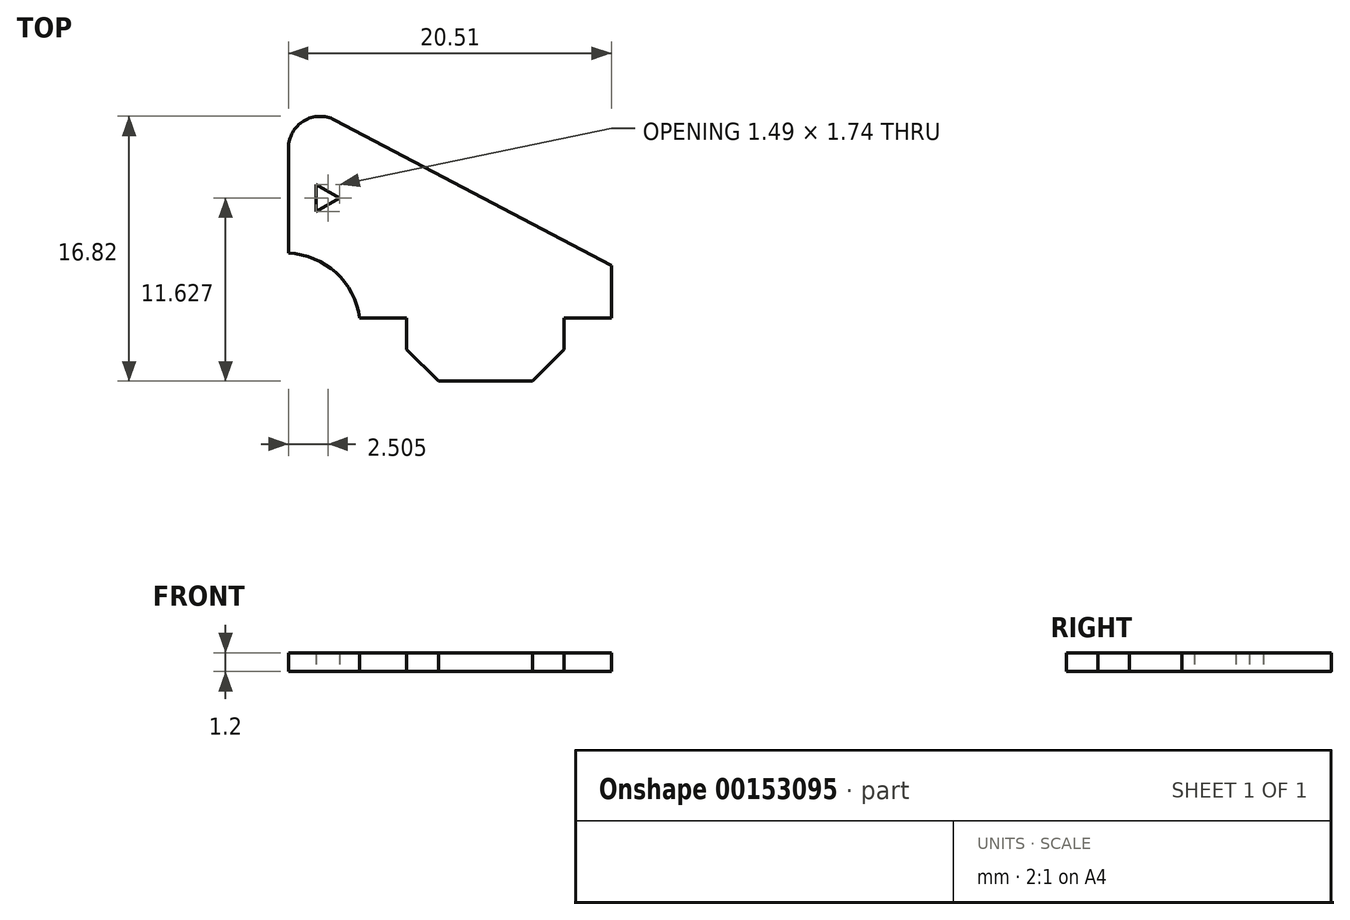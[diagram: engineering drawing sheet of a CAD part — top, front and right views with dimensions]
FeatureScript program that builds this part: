
annotation { "Feature Type Name" : "Feature", "Feature Type Description" : "" }
export const myFeature = defineFeature(function(context is Context, id is Id, definition is map)
    precondition{}
    {
        {
            var Q0;
            Q0=qCreatedBy(makeId("Top.planeOp"),FACE);
            var sketch = newSketch(context, id + "F0", { "sketchPlane" : qUnion([Q0])});
            skLineSegment(sketch, "E0", {"start": v(-14.2, 8.73) * mm, "end": v(-11.2, 8.73) * mm});
            skLineSegment(sketch, "E1", {"start": v(-11.2, 8.73) * mm, "end": v(-11.2, 6.73) * mm});
            skLineSegment(sketch, "E2", {"start": v(-11.2, 6.73) * mm, "end": v(-11.2, 4.73) * mm, "construction": true});
            skLineSegment(sketch, "E3", {"start": v(-11.2, 4.73) * mm, "end": v(-9.2, 4.73) * mm, "construction": true});
            skLineSegment(sketch, "E4", {"start": v(-11.2, 8.73) * mm, "end": v(-1.2, 8.73) * mm, "construction": true});
            skLineSegment(sketch, "E5", {"start": v(-1.2, 8.73) * mm, "end": v(1.8, 8.73) * mm});
            skLineSegment(sketch, "E6", {"start": v(-1.2, 8.73) * mm, "end": v(-1.2, 6.73) * mm});
            skLineSegment(sketch, "E7", {"start": v(-1.2, 6.73) * mm, "end": v(-1.2, 4.73) * mm, "construction": true});
            skLineSegment(sketch, "E8", {"start": v(-1.2, 4.73) * mm, "end": v(-3.2, 4.73) * mm, "construction": true});
            skLineSegment(sketch, "E9", {"start": v(-9.2, 4.73) * mm, "end": v(-3.2, 4.73) * mm});
            skLineSegment(sketch, "E10", {"start": v(-1.2, 6.73) * mm, "end": v(-3.2, 4.73) * mm});
            skLineSegment(sketch, "E11", {"start": v(1.8, 8.73) * mm, "end": v(1.8, 12.07) * mm});
            skCircle(sketch, "E12", {"center": v(-1.2, 8.73) * mm, "radius": 22.5 * mm, "construction": true});
            skCircle(sketch, "E13", {"center": v(-11.2, 8.73) * mm, "radius": 16 * mm, "construction": true});
            skLineSegment(sketch, "E14", {"start": v(1.8, 12.07) * mm, "end": v(-15.79, 21.32) * mm});
            skLineSegment(sketch, "E15", {"start": v(-18.72, 19.55) * mm, "end": v(-18.72, 12.86) * mm, "construction": true});
            skArc(sketch, "E16", {"start": v(-14.2, 8.73) * mm, "mid": v(-15.7, 11.62) * mm, "end": v(-18.72, 12.86) * mm});
            skPoint(sketch, "E17.visualSharp", {"position": v(-18.72, 22.86) * mm});
            skArc(sketch, "E17.filletArc", {"start": v(-15.79, 21.32) * mm, "mid": v(-17.75, 21.26) * mm, "end": v(-18.72, 19.55) * mm});
            skLineSegment(sketch, "E18", {"start": v(-18.72, 19.55) * mm, "end": v(-18.72, 12.86) * mm});
            skCircle(sketch, "E19", {"center": v(-18.72, 12.86) * mm, "radius": 3.5 * mm, "construction": true});
            skLineSegment(sketch, "E20", {"start": v(-18.72, 16.36) * mm, "end": v(-16.47, 16.36) * mm, "construction": true});
            skCircle(sketch, "E21", {"center": v(-16.47, 16.36) * mm, "radius": 1 * mm, "construction": true});
            skLineSegment(sketch, "E22", {"start": v(-11.2, 6.73) * mm, "end": v(-9.2, 4.73) * mm});
            skLineSegment(sketch, "E23", {"start": v(-16.96, 17.23) * mm, "end": v(-16.96, 15.49) * mm});
            skLineSegment(sketch, "E24", {"start": v(-16.96, 15.49) * mm, "end": v(-15.47, 16.34) * mm});
            skLineSegment(sketch, "E25", {"start": v(-15.47, 16.34) * mm, "end": v(-16.96, 17.23) * mm});
            skSolve(sketch);
        }
        {
            var Q0;
            Q0=makeQuery(id+"F0.imprint","IMPRINT",FACE,{"disambiguationData":[TD([[makeQuery(id+"F0.imprint","IMPRINT",EDGE,{"derivedFrom":sQuery(id+"F0.wireOp",EDGE,"E0")}),1.0]])]});
            extrude(context, id + "F1", {"entities" : qUnion([Q0]), "depth" : 1.2 * mm});
        }
    });
